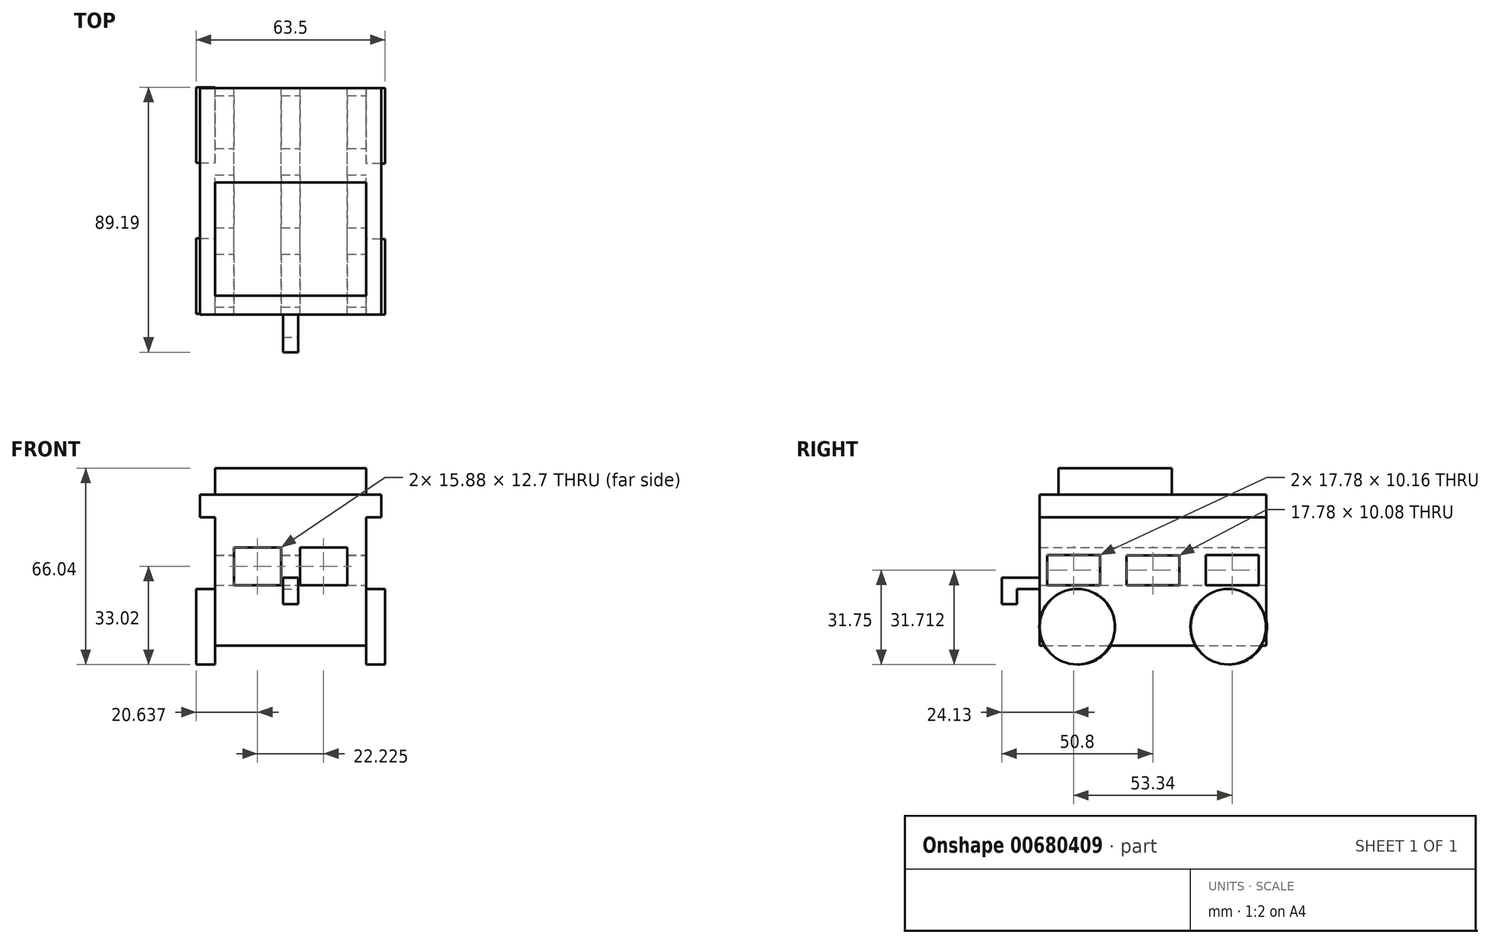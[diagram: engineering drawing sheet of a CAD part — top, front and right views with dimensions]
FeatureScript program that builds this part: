
annotation { "Feature Type Name" : "Feature", "Feature Type Description" : "" }
export const myFeature = defineFeature(function(context is Context, id is Id, definition is map)
    precondition{}
    {
        {
            var Q0;
            Q0=qCreatedBy(makeId("Front.planeOp"),FACE);
            var sketch = newSketch(context, id + "F0", { "sketchPlane" : qUnion([Q0])});
            skLineSegment(sketch, "E0", {"start": v(0, 50.8) * mm, "end": v(55.88, 50.8) * mm});
            skLineSegment(sketch, "E1", {"start": v(55.88, 50.8) * mm, "end": v(55.88, 43.18) * mm});
            skLineSegment(sketch, "E2", {"start": v(55.88, 43.18) * mm, "end": v(50.8, 43.18) * mm});
            skLineSegment(sketch, "E3", {"start": v(50.8, 43.18) * mm, "end": v(50.8, 0) * mm});
            skLineSegment(sketch, "E4", {"start": v(50.8, 0) * mm, "end": v(0, 0) * mm});
            skLineSegment(sketch, "E5", {"start": v(0, 0) * mm, "end": v(0, 43.18) * mm});
            skLineSegment(sketch, "E6", {"start": v(0, 43.18) * mm, "end": v(-5.08, 43.18) * mm});
            skLineSegment(sketch, "E7", {"start": v(-5.08, 43.18) * mm, "end": v(-5.08, 50.8) * mm});
            skLineSegment(sketch, "E8", {"start": v(-5.08, 50.8) * mm, "end": v(0, 50.8) * mm});
            skSolve(sketch);
        }
        {
            var Q0;
            Q0=makeQuery(id+"F0.imprint","IMPRINT",FACE,{"disambiguationData":[TD([[makeQuery(id+"F0.imprint","IMPRINT",EDGE,{"derivedFrom":sQuery(id+"F0.wireOp",EDGE,"E0")}),-1.0]])]});
            extrude(context, id + "F1", {"entities" : qUnion([Q0]), "depth" : 76.2 * mm});
        }
        {
            var Q0;
            Q0=makeQuery(id+"F1.opExtrude","SWEPT_FACE",FACE,{"disambiguationData":[OSD([sQuery(id+"F0.wireOp",EDGE,"E3")])]});
            var sketch = newSketch(context, id + "F2", { "sketchPlane" : qUnion([Q0])});
            skLineSegment(sketch, "E9.bottom", {"start": v(-73.66, 30.48) * mm, "end": v(-55.88, 30.48) * mm});
            skLineSegment(sketch, "E9.top", {"start": v(-73.66, 20.32) * mm, "end": v(-55.88, 20.32) * mm});
            skLineSegment(sketch, "E9.left", {"start": v(-73.66, 30.48) * mm, "end": v(-73.66, 20.32) * mm});
            skLineSegment(sketch, "E9.right", {"start": v(-55.88, 30.48) * mm, "end": v(-55.88, 20.32) * mm});
            skLineSegment(sketch, "E10.bottom", {"start": v(-46.99, 30.4) * mm, "end": v(-29.2, 30.4) * mm});
            skLineSegment(sketch, "E10.top", {"start": v(-46.99, 20.32) * mm, "end": v(-29.2, 20.32) * mm});
            skLineSegment(sketch, "E10.left", {"start": v(-46.99, 30.4) * mm, "end": v(-46.99, 20.32) * mm});
            skLineSegment(sketch, "E10.right", {"start": v(-29.21, 30.4) * mm, "end": v(-29.21, 20.32) * mm});
            skLineSegment(sketch, "E11.bottom", {"start": v(-20.32, 30.48) * mm, "end": v(-2.54, 30.48) * mm});
            skLineSegment(sketch, "E11.top", {"start": v(-20.32, 20.32) * mm, "end": v(-2.54, 20.32) * mm});
            skLineSegment(sketch, "E11.left", {"start": v(-20.32, 30.48) * mm, "end": v(-20.32, 20.32) * mm});
            skLineSegment(sketch, "E11.right", {"start": v(-2.54, 30.48) * mm, "end": v(-2.54, 20.32) * mm});
            skSolve(sketch);
        }
        {
            var Q0;
            Q0=makeQuery(id+"F2.imprint","IMPRINT",FACE,{"disambiguationData":[TD([[makeQuery(id+"F2.imprint","IMPRINT",EDGE,{"derivedFrom":sQuery(id+"F2.wireOp",EDGE,"E9.bottom")}),-1.0]])]});
            var Q1;
            Q1=makeQuery(id+"F2.imprint","IMPRINT",FACE,{"disambiguationData":[TD([[makeQuery(id+"F2.imprint","IMPRINT",EDGE,{"derivedFrom":sQuery(id+"F2.wireOp",EDGE,"E10.bottom")}),-1.0]])]});
            var Q2;
            Q2=makeQuery(id+"F2.imprint","IMPRINT",FACE,{"disambiguationData":[TD([[makeQuery(id+"F2.imprint","IMPRINT",EDGE,{"derivedFrom":sQuery(id+"F2.wireOp",EDGE,"E11.bottom")}),-1.0]])]});
            extrude(context, id + "F3", {"entities" : qUnion([Q0, Q1, Q2]), "operationType" : NewBodyOperationType.REMOVE, "oppositeDirection" : true, "depth" : 50.8 * mm});
        }
        {
            var Q0;
            Q0=makeQuery(id+"F1.opExtrude","SWEPT_FACE",FACE,{"disambiguationData":[OSD([sQuery(id+"F0.wireOp",EDGE,"E3")])]});
            var sketch = newSketch(context, id + "F4", { "sketchPlane" : qUnion([Q0])});
            skCircle(sketch, "E12", {"center": v(-63.53, 6.35) * mm, "radius": 12.7 * mm});
            skCircle(sketch, "E13", {"center": v(-12.73, 6.35) * mm, "radius": 12.7 * mm});
            skSolve(sketch);
        }
        {
            var Q0;
            Q0=qSketchRegion(id+"F4",true);
            extrude(context, id + "F5", {"entities" : qUnion([Q0]), "depth" : 6.35 * mm});
        }
        {
            var Q0;
            Q0=makeQuery(id+"F1.opExtrude","SWEPT_FACE",FACE,{"disambiguationData":[OSD([sQuery(id+"F0.wireOp",EDGE,"E5")])]});
            var sketch = newSketch(context, id + "F6", { "sketchPlane" : qUnion([Q0])});
            skCircle(sketch, "E14", {"center": v(63.21, 6.35) * mm, "radius": 12.7 * mm});
            skCircle(sketch, "E15", {"center": v(12.41, 6.35) * mm, "radius": 12.7 * mm});
            skSolve(sketch);
        }
        {
            var Q0;
            Q0=makeQuery(id+"F1.opExtrude","CAP_FACE",FACE,{"disambiguationData":[OSD([sQuery(id+"F0.wireOp",EDGE,"E0"),sQuery(id+"F0.wireOp",EDGE,"E1"),sQuery(id+"F0.wireOp",EDGE,"E2"),sQuery(id+"F0.wireOp",EDGE,"E3"),sQuery(id+"F0.wireOp",EDGE,"E4"),sQuery(id+"F0.wireOp",EDGE,"E5"),sQuery(id+"F0.wireOp",EDGE,"E6"),sQuery(id+"F0.wireOp",EDGE,"E7"),sQuery(id+"F0.wireOp",EDGE,"E8")])],"isStart":true});
            var sketch = newSketch(context, id + "F7", { "sketchPlane" : qUnion([Q0])});
            skLineSegment(sketch, "E16.bottom", {"start": v(-44.45, 33.02) * mm, "end": v(-28.57, 33.02) * mm});
            skLineSegment(sketch, "E16.top", {"start": v(-44.45, 20.32) * mm, "end": v(-28.57, 20.32) * mm});
            skLineSegment(sketch, "E16.left", {"start": v(-44.45, 33.02) * mm, "end": v(-44.45, 20.32) * mm});
            skLineSegment(sketch, "E16.right", {"start": v(-28.57, 33.02) * mm, "end": v(-28.57, 20.32) * mm});
            skLineSegment(sketch, "E17.bottom", {"start": v(-22.22, 33.02) * mm, "end": v(-6.35, 33.02) * mm});
            skLineSegment(sketch, "E17.top", {"start": v(-22.22, 20.32) * mm, "end": v(-6.35, 20.32) * mm});
            skLineSegment(sketch, "E17.left", {"start": v(-22.22, 33.02) * mm, "end": v(-22.22, 20.32) * mm});
            skLineSegment(sketch, "E17.right", {"start": v(-6.35, 33.02) * mm, "end": v(-6.35, 20.32) * mm});
            skSolve(sketch);
        }
        {
            var Q0;
            Q0=makeQuery(id+"F7.imprint","IMPRINT",FACE,{"disambiguationData":[TD([[makeQuery(id+"F7.imprint","IMPRINT",EDGE,{"derivedFrom":sQuery(id+"F7.wireOp",EDGE,"E16.bottom")}),-1.0]])]});
            var Q1;
            Q1=makeQuery(id+"F7.imprint","IMPRINT",FACE,{"disambiguationData":[TD([[makeQuery(id+"F7.imprint","IMPRINT",EDGE,{"derivedFrom":sQuery(id+"F7.wireOp",EDGE,"E17.bottom")}),-1.0]])]});
            extrude(context, id + "F8", {"entities" : qUnion([Q0, Q1]), "operationType" : NewBodyOperationType.REMOVE, "oppositeDirection" : true, "depth" : 76.2 * mm});
        }
        {
            var Q0;
            Q0=makeQuery(id+"F1.opExtrude","SWEPT_FACE",FACE,{"disambiguationData":[OSD([sQuery(id+"F0.wireOp",EDGE,"E0"),sQuery(id+"F0.wireOp",EDGE,"E8")])]});
            var sketch = newSketch(context, id + "F9", { "sketchPlane" : qUnion([Q0])});
            skPoint(sketch, "E18.end.orphan", {"position": v(55.88, -38.1) * mm});
            skPoint(sketch, "E19.start.orphan", {"position": v(-5.08, -38.1) * mm});
            skLineSegment(sketch, "E20.bottom", {"start": v(0, -31.75) * mm, "end": v(50.8, -31.75) * mm});
            skLineSegment(sketch, "E20.top", {"start": v(0, -69.85) * mm, "end": v(50.8, -69.85) * mm});
            skLineSegment(sketch, "E20.left", {"start": v(0, -31.75) * mm, "end": v(0, -69.85) * mm});
            skLineSegment(sketch, "E20.right", {"start": v(50.8, -31.75) * mm, "end": v(50.8, -69.85) * mm});
            skSolve(sketch);
        }
        {
            var Q0;
            Q0=makeQuery(id+"F9.imprint","IMPRINT",FACE,{"disambiguationData":[TD([[makeQuery(id+"F9.imprint","IMPRINT",EDGE,{"derivedFrom":sQuery(id+"F9.wireOp",EDGE,"E20.bottom")}),-1.0]])]});
            extrude(context, id + "F10", {"entities" : qUnion([Q0]), "depth" : 8.9 * mm});
        }
        {
            var Q0;
            Q0=makeQuery(id+"F1.opExtrude","SWEPT_FACE",FACE,{"disambiguationData":[OSD([sQuery(id+"F0.wireOp",EDGE,"E3")])]});
            var sketch = newSketch(context, id + "F11", { "sketchPlane" : qUnion([Q0])});
            skLineSegment(sketch, "E21", {"start": v(-76.2, 22.86) * mm, "end": v(-88.9, 22.86) * mm});
            skLineSegment(sketch, "E22", {"start": v(-88.9, 22.86) * mm, "end": v(-88.9, 13.97) * mm});
            skLineSegment(sketch, "E23", {"start": v(-88.9, 13.97) * mm, "end": v(-83.82, 13.97) * mm});
            skLineSegment(sketch, "E24", {"start": v(-83.82, 13.97) * mm, "end": v(-83.82, 19.05) * mm});
            skLineSegment(sketch, "E25", {"start": v(-83.82, 19.05) * mm, "end": v(-76.2, 19.05) * mm});
            skLineSegment(sketch, "E26", {"start": v(-76.2, 19.05) * mm, "end": v(-76.2, 22.86) * mm});
            skSolve(sketch);
        }
        {
            var Q0;
            Q0=makeQuery(id+"F11.imprint","IMPRINT",FACE,{"disambiguationData":[TD([[makeQuery(id+"F11.imprint","IMPRINT",EDGE,{"derivedFrom":sQuery(id+"F11.wireOp",EDGE,"E21")}),1.0]])]});
            extrude(context, id + "F12", {"entities" : qUnion([Q0]), "operationType" : NewBodyOperationType.ADD, "oppositeDirection" : true, "depth" : 27.94 * mm});
        }
        {
            var Q0;
            Q0=qSketchRegion(id+"F11",true);
            extrude(context, id + "F13", {"entities" : qUnion([Q0]), "operationType" : NewBodyOperationType.REMOVE, "oppositeDirection" : true, "depth" : 22.86 * mm});
        }
        {
            var Q0;
            Q0=qSketchRegion(id+"F6",true);
            extrude(context, id + "F14", {"entities" : qUnion([Q0]), "depth" : 6.35 * mm});
        }
    });
